# Revit family: Plumbing-Faucet-Sloan-Valve-EFX-377
name_source: partatom
category: Plumbing Fixtures
units: mm (PartAtom-declared; Revit-internal decimal feet)

## family parameters
Cut with Voids When Loaded = No
Host = Face
Maintain Annotation Orientation = No
OmniClass Number = 23.45.55.14
OmniClass Title = Single Faucets
Part Type = Normal
Room Calculation Point = No
Round Connector Dimension = Use Diameter
Shared = No

## types (8) — shared parameters
Assembly Code = D2010
CW Connection = Yes
CWFU = 1.5
Cold Water Connection Diameter = 0"
Default Elevation = 0"
Depth = 6"
Edition number = 1
HW Connection = Yes
HWFU = 1.5
Height = 5"
Hot Water Connection Diameter = 0"
Hot Water Connector Description = Hot Water Connection
Keynote = 15410
Manufacturer = Sloan Valve
Product Material = Sloan Valve - Finish - Polished Chrome
Product data url = https://bimobject.com
URL = www.sloanvalve.com
Valve Pressure Drop = 0.00 psi
Vent Connection = No
Waste Connection = No
z_Trim Plate Length = 10 1/4"
zero-valued in all types: WFU

## per-type parameters (varying)
| type | Description | Part Number | Water Flow | Width | z_No Trim Plate | z_Trim Plate 8 |
| EFX-377-SOL-ISM-CP-0.5GPM-MLM-IR-FCT | Solar Power Supply, Integrated Side Mixer, Polished Chrome Finish, 0.5 gpm, Multi-Laminar Spray, Infrared Sensor, BASYS® SolarPowered Deck-Mounted Low Body Guided Handwashing Display. | 3324272 | 1 GPM | 2 1/2" | Yes | No |
| EFX-377-8-SOL-TEE-CP-0.5GPM-MLM-IR-FCT | 8" Trim Plate, Solar Power Supply, Back-Check Tee, Polished Chrome Finish, 0.5 gpm, Multi-Laminar Spray, Infrared Sensor, BASYS® SolarPowered Deck-Mounted Low Body Guided Handwashing Display. | 3324256 | 1 GPM | 10 1/4" | No | Yes |
| EFX-377-SOL-ISM-CP-1.5GPM-IR-FCT | Solar Power Supply, Integrated Side Mixer, Polished Chrome Finish, 1.5 gpm, Aerated (installed) or Laminar (in box) Spray, Infrared Sensor, BASYS® Solar-Powered Deck-Mounted Low Body Guided Handwashing Display. | 3324273 | 2 GPM | 2 1/2" | Yes | No |
| EFX-377-SOL-ISM-CP-1.5GPM-MLM-IR-FCT | Solar Power Supply, Integrated Side Mixer, Polished Chrome Finish, 1.5 gpm, Multi-Laminar Spray, Infrared Sensor, BASYS® SolarPowered Deck-Mounted Low Body Guided Handwashing Display. | 3324317 | 2 GPM | 2 1/2" | Yes | No |
| EFX-377-SOL-TEE-CP-0.5GPM-MLM-IR-FCT | Solar Power Supply, Back-Check Tee, Polished Chrome Finish, 0.5 gpm, Multi-Laminar Spray, Infrared Sensor, BASYS® Solar-Powered Deck-Mounted Low Body Guided Handwashing Display. | 3324255 | 1 GPM | 2 1/2" | Yes | No |
| EFX-377-SOL-ISM-CP-0.35GPM-MLM-IR-FCT | Solar Power Supply, Integrated Side Mixer, Polished Chrome Finish, 0.35 gpm, Multi-Laminar Spray, Infrared Sensor, BASYS® SolarPowered Deck-Mounted Low Body Guided Handwashing Display. | 33243173 | 0 GPM | 2 1/2" | Yes | No |
| EFX-377-8-SOL-TEE-CP-0.35GPM-MLM-IR-FCT | 8" Trim Plate, Solar Power Supply, Back-Check Tee, Polished Chrome Finish, 0.35 gpm, Multi-Laminar Spray, Infrared Sensor, BASYS® SolarPowered Deck-Mounted Low Body Guided Handwashing Display. | 33243172 | 0 GPM | 10 1/4" | No | Yes |
| EFX-377-SOL-TEE-CP-0.35GPM-MLM-IR-FCT | Solar Power Supply, Back-Check Tee, Polished Chrome Finish, 0.35 gpm, Multi-Laminar Spray, Infrared Sensor, BASYS® Solar-Powered Deck-Mounted Low Body Guided Handwashing Display. | 33243174 | 0 GPM | 2 1/2" | Yes | No |

note: column(s) folded — value = type name in every type: Model

## geometry (parser evidence)
native form markers: Sweep x13
no freeform markers — native parametric forms only
